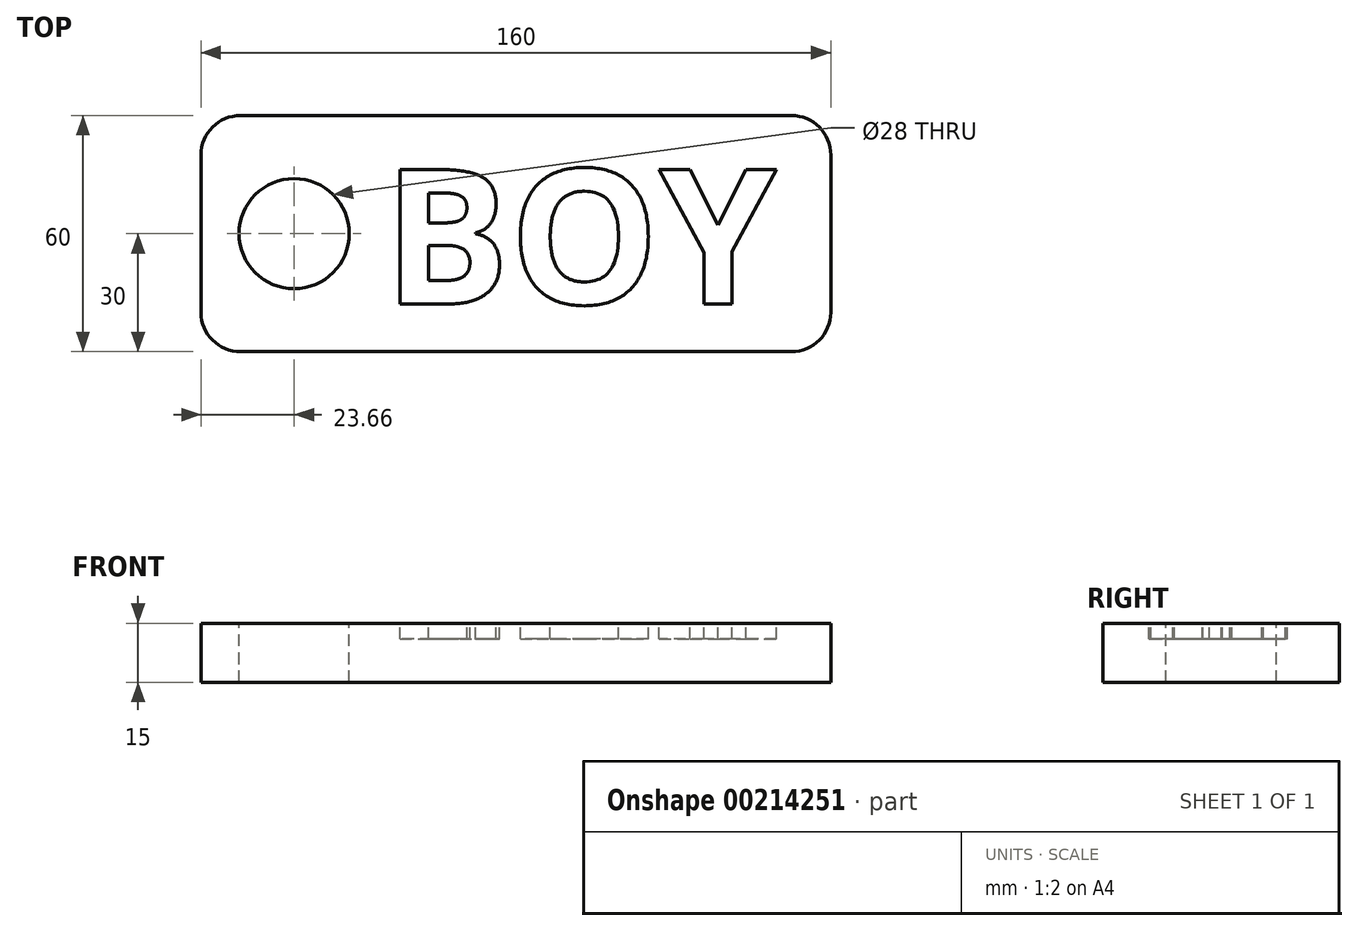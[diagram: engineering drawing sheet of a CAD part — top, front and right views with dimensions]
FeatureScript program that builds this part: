
annotation { "Feature Type Name" : "Feature", "Feature Type Description" : "" }
export const myFeature = defineFeature(function(context is Context, id is Id, definition is map)
    precondition{}
    {
        {
            var Q0;
            Q0=qCreatedBy(makeId("Top.planeOp"),FACE);
            var sketch = newSketch(context, id + "F0", { "sketchPlane" : qUnion([Q0])});
            skLineSegment(sketch, "E0.bottom", {"start": v(-80, 30) * mm, "end": v(80, 30) * mm});
            skLineSegment(sketch, "E0.top", {"start": v(-80, -30) * mm, "end": v(80, -30) * mm});
            skLineSegment(sketch, "E0.left", {"start": v(-80, 30) * mm, "end": v(-80, -30) * mm});
            skLineSegment(sketch, "E0.right", {"start": v(80, 30) * mm, "end": v(80, -30) * mm});
            skPoint(sketch, "E0.middle", {"position": v(0, 0) * mm});
            skLineSegment(sketch, "E1", {"start": v(-80, 0) * mm, "end": v(80, 0) * mm, "construction": true});
            skLineSegment(sketch, "E2", {"start": v(0, 30) * mm, "end": v(0, -30) * mm, "construction": true});
            skSolve(sketch);
        }
        {
            var Q0;
            Q0=makeQuery(id+"F0.imprint","IMPRINT",FACE,{"disambiguationData":[TD([[makeQuery(id+"F0.imprint","IMPRINT",EDGE,{"derivedFrom":sQuery(id+"F0.wireOp",EDGE,"E0.bottom")}),-1.0]])]});
            extrude(context, id + "F1", {"entities" : qUnion([Q0]), "depth" : 8 * mm});
        }
        {
            var Q0;
            Q0=makeQuery(id+"F1.opExtrude","CAP_FACE",FACE,{"disambiguationData":[OSD([sQuery(id+"F0.wireOp",EDGE,"E0.bottom"),sQuery(id+"F0.wireOp",EDGE,"E0.top"),sQuery(id+"F0.wireOp",EDGE,"E0.left"),sQuery(id+"F0.wireOp",EDGE,"E0.right")])],"isStart":false});
            var sketch = newSketch(context, id + "F2", { "sketchPlane" : qUnion([Q0])});
            skCircle(sketch, "E3", {"center": v(-56.34, 0) * mm, "radius": 14 * mm});
            skSolve(sketch);
        }
        {
            var Q0;
            Q0=makeQuery(id+"F2.imprint","IMPRINT",FACE,{"disambiguationData":[TD([[makeQuery(id+"F2.imprint","IMPRINT",EDGE,{"derivedFrom":sQuery(id+"F2.wireOp",EDGE,"E3")}),1.0]])]});
            extrude(context, id + "F3", {"entities" : qUnion([Q0]), "operationType" : NewBodyOperationType.REMOVE, "oppositeDirection" : true, "depth" : 25 * mm});
        }
        {
            var Q0;
            Q0=makeQuery(id+"F1.opExtrude","CAP_FACE",FACE,{"disambiguationData":[OSD([sQuery(id+"F0.wireOp",EDGE,"E0.bottom"),sQuery(id+"F0.wireOp",EDGE,"E0.top"),sQuery(id+"F0.wireOp",EDGE,"E0.left"),sQuery(id+"F0.wireOp",EDGE,"E0.right")])],"isStart":false});
            extrude(context, id + "F4", {"entities" : qUnion([Q0]), "operationType" : NewBodyOperationType.ADD, "depth" : 7 * mm});
        }
        {
            var Q0;
            {var subQ0=sQuery(id+"F0.wireOp",EDGE,"E0.left");var subQ1=sQuery(id+"F0.wireOp",EDGE,"E0.top");Q0=makeQuery(id+"F4.boolean.opBoolean","MERGE",EDGE,{"derivedFrom":[makeQuery(id+"F1.opExtrude","SWEPT_EDGE",EDGE,{"disambiguationData":[OSD([subQ1,subQ0])]}),makeQuery(id+"F4.opExtrude","SWEPT_EDGE",EDGE,{"disambiguationData":[OSD([subQ1,subQ0])]})]});}
            var Q1;
            {var subQ0=sQuery(id+"F0.wireOp",EDGE,"E0.right");var subQ1=sQuery(id+"F0.wireOp",EDGE,"E0.top");Q1=makeQuery(id+"F4.boolean.opBoolean","MERGE",EDGE,{"derivedFrom":[makeQuery(id+"F1.opExtrude","SWEPT_EDGE",EDGE,{"disambiguationData":[OSD([subQ1,subQ0])]}),makeQuery(id+"F4.opExtrude","SWEPT_EDGE",EDGE,{"disambiguationData":[OSD([subQ1,subQ0])]})]});}
            var Q2;
            {var subQ0=sQuery(id+"F0.wireOp",EDGE,"E0.right");var subQ1=sQuery(id+"F0.wireOp",EDGE,"E0.bottom");Q2=makeQuery(id+"F4.boolean.opBoolean","MERGE",EDGE,{"derivedFrom":[makeQuery(id+"F1.opExtrude","SWEPT_EDGE",EDGE,{"disambiguationData":[OSD([subQ1,subQ0])]}),makeQuery(id+"F4.opExtrude","SWEPT_EDGE",EDGE,{"disambiguationData":[OSD([subQ1,subQ0])]})]});}
            var Q3;
            {var subQ0=sQuery(id+"F0.wireOp",EDGE,"E0.left");var subQ1=sQuery(id+"F0.wireOp",EDGE,"E0.bottom");Q3=makeQuery(id+"F4.boolean.opBoolean","MERGE",EDGE,{"derivedFrom":[makeQuery(id+"F1.opExtrude","SWEPT_EDGE",EDGE,{"disambiguationData":[OSD([subQ1,subQ0])]}),makeQuery(id+"F4.opExtrude","SWEPT_EDGE",EDGE,{"disambiguationData":[OSD([subQ1,subQ0])]})]});}
            fillet(context, id + "F5", {"entities" : qUnion([Q0, Q1, Q2, Q3]), "radius" : 10 * mm, "tangentPropagation" : true, "allowEdgeOverflow" : false});
        }
        {
            var Q0;
            Q0=makeQuery(id+"F4.opExtrude","CAP_FACE",FACE,{"disambiguationData":[OSD([sQuery(id+"F0.wireOp",EDGE,"E0.bottom"),sQuery(id+"F0.wireOp",EDGE,"E0.top"),sQuery(id+"F0.wireOp",EDGE,"E0.left"),sQuery(id+"F0.wireOp",EDGE,"E0.right")])],"isStart":false});
            var sketch = newSketch(context, id + "F6", { "sketchPlane" : qUnion([Q0])});
            skSolve(sketch);
        }
        {
            var Q0;
            Q0=makeQuery(id+"F6.imprint","IMPRINT",FACE,{"disambiguationData":[TD([[makeQuery(id+"F6.imprint","IMPRINT",EDGE,{"derivedFrom":makeQuery(id+"F4.opExtrude","CAP_EDGE",EDGE,{"disambiguationData":[OSD([sQuery(id+"F2.wireOp",EDGE,"E3")])],"isStart":false})}),-1.0]])]});
            var sketch = newSketch(context, id + "F7", { "sketchPlane" : qUnion([Q0])});
            skText(sketch, "E4", { "text": "BOY", "fontName": "OpenSans-Bold.ttf"});
            const initialGuessF7  = {"E4": [-0.03377, -0.01786, 1, 0, 0.03442]};
            skSetInitialGuess(sketch, initialGuessF7);
            skSolve(sketch);
        }
        {
            var Q0;
            Q0 = qSketchRegion(id + "F7", true);
            extrude(context, id + "F8", {"entities" : qUnion([Q0]), "operationType" : NewBodyOperationType.REMOVE, "oppositeDirection" : true, "depth" : 4 * mm});
        }
    });
